# Revit family: DC_Rheem_PLM_940080
name_source: partatom
category: Plumbing Fixtures
revit_build: Autodesk Revit 2017 (Build: 20160225_1515(x64)
units: mm (PartAtom-declared; Revit-internal decimal feet)

## family parameters
Cut with Voids When Loaded = No
Host = Face
Part Type = Normal
Room Calculation Point = No
Round Connector Dimension = Use Radius
Shared = No

## types (1)
- Guardian Warm Water 80L/min nominated flow rate
    ARMRadius_ANZRS = 20 mm  [stored 0.0656168 ft]
    ARMWaterDiameter_ANZRS = 40 mm  [stored 0.131234 ft]
    BoxHeight_ANZRS = 650 mm
    BoxThickness_ANZRS = 350 mm
    BoxWidth_ANZRS = 600 mm
    ColdWaterPipeDiameter_ANZRS = 25 mm  [stored 0.082021 ft]
    ColdWaterSupplyRadius_ANZRS = 13 mm
    Default Elevation = 0 mm  [stored 0 ft]
    Description = Guardian Warm Water 80L/min nominated flow rate
    HotWaterPipeDiameter_ANZRS = 40 mm  [stored 0.131234 ft]
    HotWaterSupplyRadius_ANZRS = 20 mm  [stored 0.0656168 ft]
    Manufacturer = Rheem
    Materials_ANZRS = Rheem - Stainless Steel
    Model = 940080
    Type Comments = Temperature range 25-60°C
    URL = http://www.rheem.com.au
    WWR_ANZRS = 25 mm  [stored 0.082021 ft]
    WarmWaterPipeDiameter_ANZRS = 50 mm  [stored 0.164042 ft]

note: [stored X ft] marks values corroborated as IEEE doubles in the binary element streams (Revit-internal decimal feet)

## geometry (parser evidence)
native form markers: Blend x6, Sweep x2
no freeform markers — native parametric forms only
